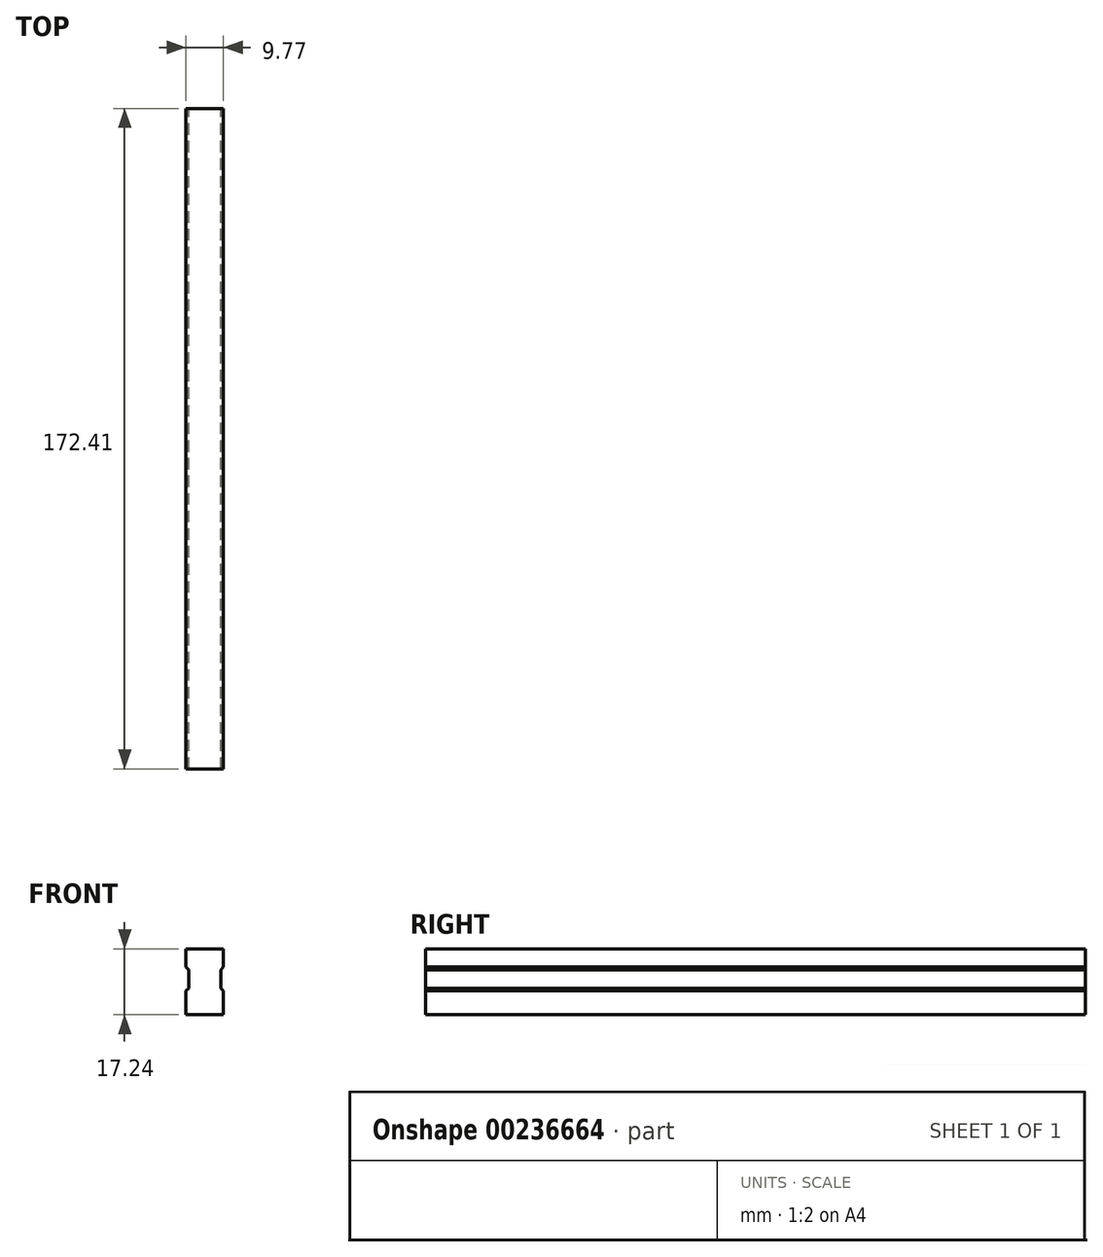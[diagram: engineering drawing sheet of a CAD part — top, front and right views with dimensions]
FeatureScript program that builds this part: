
annotation { "Feature Type Name" : "Feature", "Feature Type Description" : "" }
export const myFeature = defineFeature(function(context is Context, id is Id, definition is map)
    precondition{}
    {
        {
            assignVariable(context, id + "F0", {"name" : "scale", "anyValue" : 1 / 87});
        }
        {
            var Q0;
            Q0=qCreatedBy(makeId("Front.planeOp"),FACE);
            var sketch = newSketch(context, id + "F1", { "sketchPlane" : qUnion([Q0])});
            skLineSegment(sketch, "E0.bottom", {"start": v(0, 0) * mm, "end": v(9.77, 0) * mm, "construction": true});
            skLineSegment(sketch, "E0.top", {"start": v(0, 17.24) * mm, "end": v(9.77, 17.24) * mm, "construction": true});
            skLineSegment(sketch, "E0.left", {"start": v(0, 0) * mm, "end": v(0, 17.24) * mm, "construction": true});
            skLineSegment(sketch, "E0.right", {"start": v(9.77, 0) * mm, "end": v(9.77, 17.24) * mm, "construction": true});
            skLineSegment(sketch, "E1", {"start": v(4.89, 17.24) * mm, "end": v(4.89, 0) * mm, "construction": true});
            skLineSegment(sketch, "E2", {"start": v(4.89, 0) * mm, "end": v(0, 0) * mm});
            skLineSegment(sketch, "E3", {"start": v(0, 6.26) * mm, "end": v(0.75, 6.95) * mm});
            skLineSegment(sketch, "E4", {"start": v(0.75, 6.95) * mm, "end": v(0.75, 11.78) * mm});
            skLineSegment(sketch, "E5", {"start": v(0.75, 11.78) * mm, "end": v(0, 12.47) * mm});
            skLineSegment(sketch, "E6", {"start": v(0, 12.47) * mm, "end": v(0, 17.24) * mm});
            skLineSegment(sketch, "E7", {"start": v(4.89, 17.24) * mm, "end": v(0, 17.24) * mm});
            skLineSegment(sketch, "E8", {"start": v(0, 0) * mm, "end": v(0, 6.26) * mm});
            skLineSegment(sketch, "E9.MirrorCS", {"start": v(9.02, 11.78) * mm, "end": v(9.77, 12.47) * mm});
            skLineSegment(sketch, "E10.MirrorCS", {"start": v(9.77, 6.26) * mm, "end": v(9.02, 6.95) * mm});
            skLineSegment(sketch, "E11.MirrorCS", {"start": v(9.77, 0) * mm, "end": v(9.77, 6.26) * mm});
            skLineSegment(sketch, "E12.MirrorCS", {"start": v(4.89, 17.24) * mm, "end": v(9.77, 17.24) * mm});
            skLineSegment(sketch, "E13.MirrorCS", {"start": v(4.89, 0) * mm, "end": v(9.77, 0) * mm});
            skLineSegment(sketch, "E14.MirrorCS", {"start": v(9.02, 6.95) * mm, "end": v(9.02, 11.78) * mm});
            skLineSegment(sketch, "E15.MirrorCS", {"start": v(9.77, 12.47) * mm, "end": v(9.77, 17.24) * mm});
            skSolve(sketch);
        }
        {
            var Q0;
            Q0=makeQuery(id+"F1.imprint","IMPRINT",FACE,{"disambiguationData":[TD([[makeQuery(id+"F1.imprint","IMPRINT",EDGE,{"derivedFrom":sQuery(id+"F1.wireOp",EDGE,"E2")}),-1.0]])]});
            extrude(context, id + "F2", {"entities" : qUnion([Q0]), "depth" : 30000 * getVariable(context, 'scale') / 2 * mm});
        }
    });
